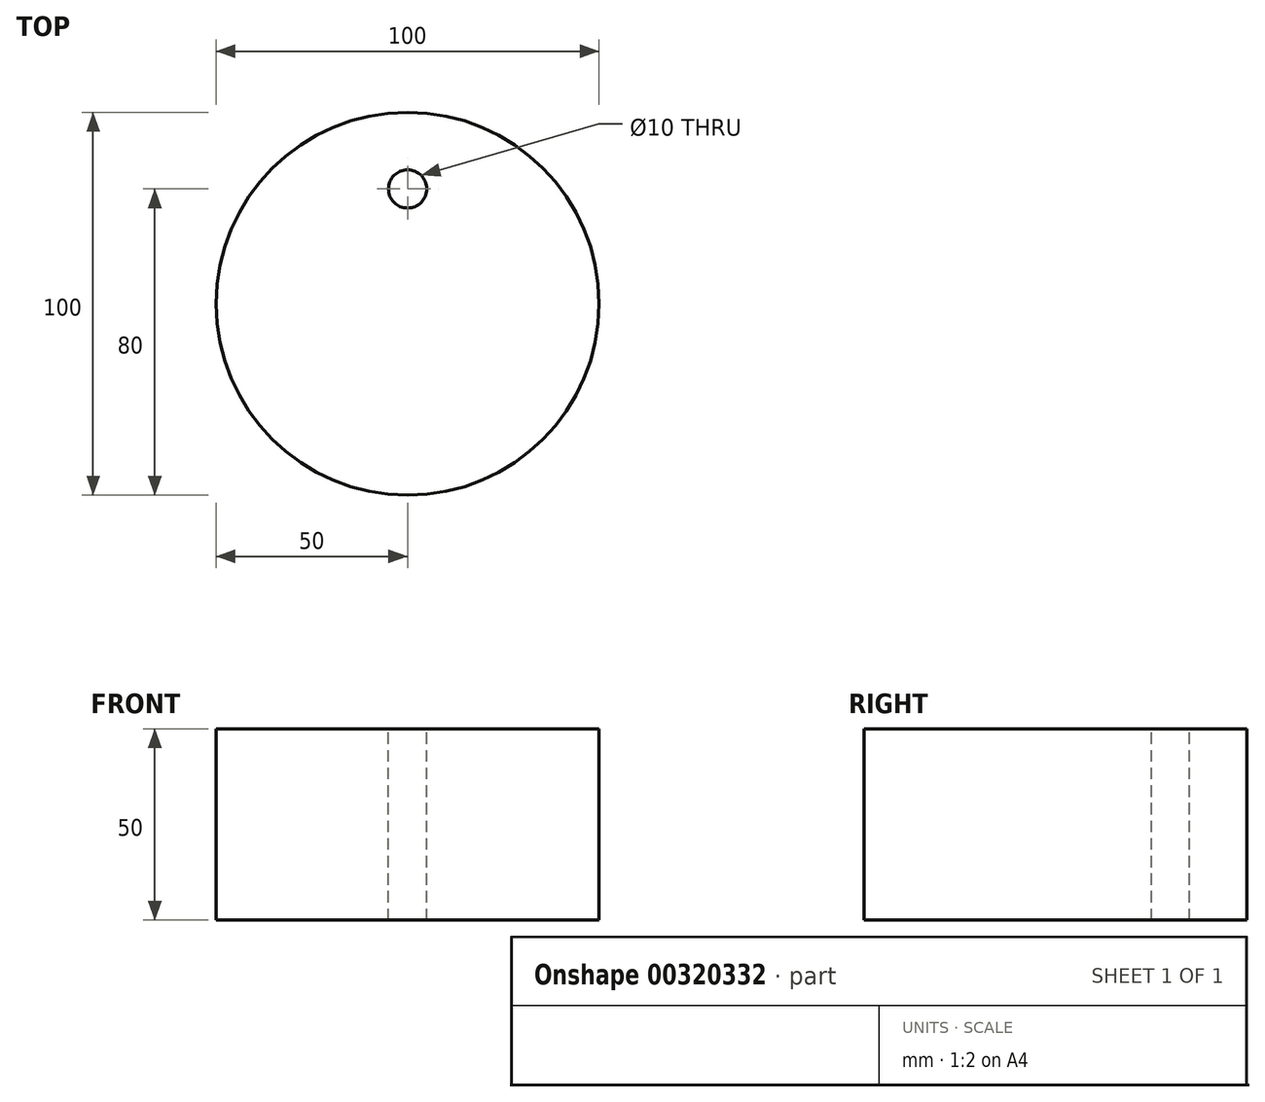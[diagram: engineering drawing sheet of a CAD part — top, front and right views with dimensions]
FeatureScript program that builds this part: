
annotation { "Feature Type Name" : "Feature", "Feature Type Description" : "" }
export const myFeature = defineFeature(function(context is Context, id is Id, definition is map)
    precondition{}
    {
        {
            var Q0;
            Q0=qCreatedBy(makeId("Top.planeOp"),FACE);
            var sketch = newSketch(context, id + "F0", { "sketchPlane" : qUnion([Q0])});
            skCircle(sketch, "E0", {"center": v(0, 0) * mm, "radius": 50 * mm});
            skSolve(sketch);
        }
        {
            var Q0;
            Q0=makeQuery(id+"F0.imprint","IMPRINT",FACE,{"disambiguationData":[TD([[makeQuery(id+"F0.imprint","IMPRINT",EDGE,{"derivedFrom":sQuery(id+"F0.wireOp",EDGE,"E0")}),1.0]])]});
            extrude(context, id + "F1", {"entities" : qUnion([Q0]), "depth" : 50 * mm});
        }
        {
            var Q0;
            Q0=makeQuery(id+"F1.opExtrude","CAP_FACE",FACE,{"disambiguationData":[OSD([sQuery(id+"F0.wireOp",EDGE,"E0")])],"isStart":false});
            var sketch = newSketch(context, id + "F2", { "sketchPlane" : qUnion([Q0])});
            skPoint(sketch, "E1", {"position": v(0, 30) * mm});
            skSolve(sketch);
        }
        {
            var Q0;
            Q0=sQuery(id+"F2.wireOp",VERTEX,"E1");
            var Q1;
            Q1=makeQuery(id+"F1.opExtrude","SWEPT_BODY",BODY,{"disambiguationData":[OSD([sQuery(id+"F0.wireOp",EDGE,"E0")])]});
            hole(context, id + "F3", {"style" : HoleStyle.SIMPLE, "endStyle" : HoleEndStyle.THROUGH, "holeDiameter" : 10 * mm, "tappedDepth" : 12 * mm, "tapClearance" : 3, "locations" : qUnion([Q0]), "scope" : qUnion([Q1])});
        }
    });
